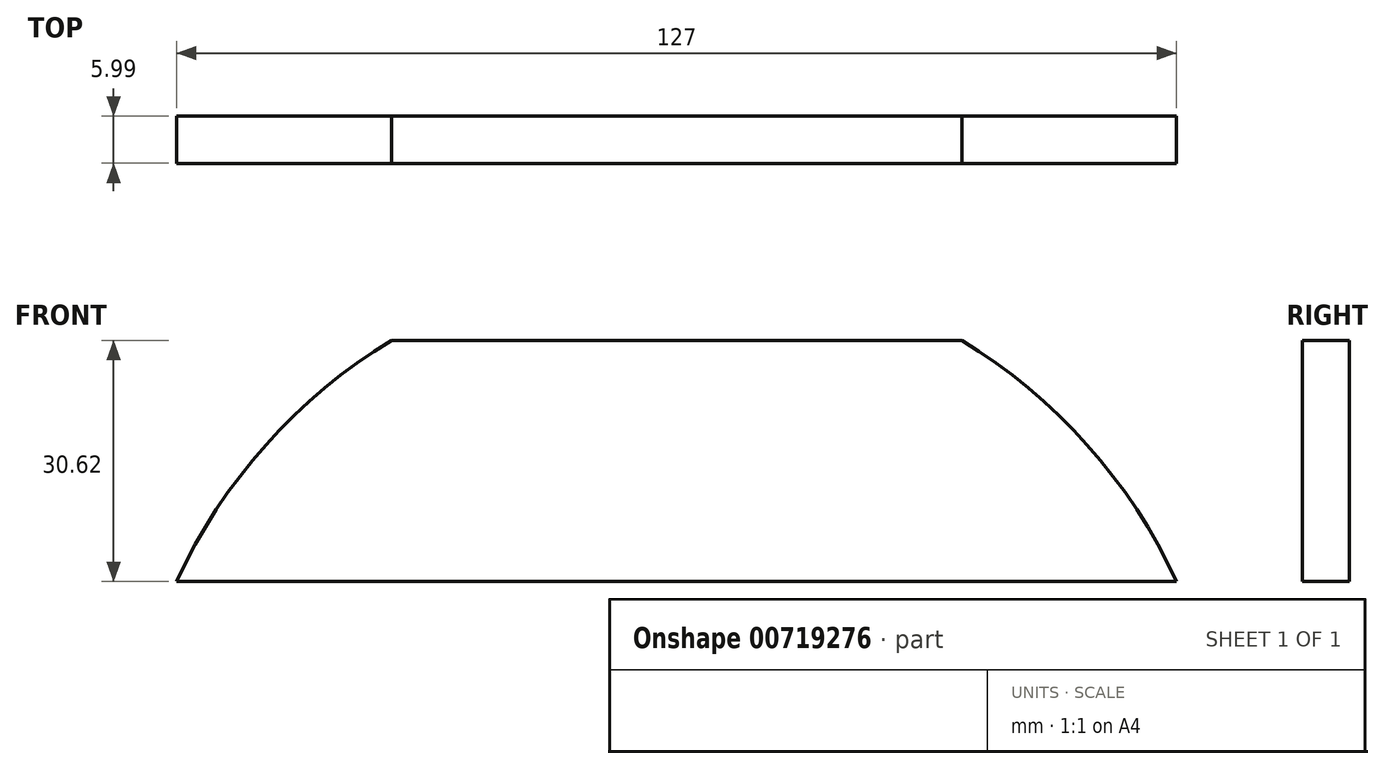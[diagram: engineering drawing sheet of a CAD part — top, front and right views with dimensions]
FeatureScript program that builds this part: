
annotation { "Feature Type Name" : "Feature", "Feature Type Description" : "" }
export const myFeature = defineFeature(function(context is Context, id is Id, definition is map)
    precondition{}
    {
        {
            var Q0;
            Q0=qCreatedBy(makeId("Front.planeOp"),FACE);
            var sketch = newSketch(context, id + "F0", { "sketchPlane" : qUnion([Q0])});
            skLineSegment(sketch, "E0", {"start": v(0, 0) * mm, "end": v(0, 29.1) * mm, "construction": true});
            skLineSegment(sketch, "E1", {"start": v(-63.5, 29.1) * mm, "end": v(-15.24, 29.1) * mm});
            skLineSegment(sketch, "E2", {"start": v(63.5, 29.1) * mm, "end": v(15.24, 29.1) * mm});
            skArc(sketch, "E3", {"start": v(63.5, 29.1) * mm, "mid": v(52.16, 46.46) * mm, "end": v(36.22, 59.72) * mm});
            skLineSegment(sketch, "E4", {"start": v(-36.22, 59.72) * mm, "end": v(36.22, 59.72) * mm});
            skArc(sketch, "E5.trimOffspring", {"start": v(-36.22, 59.72) * mm, "mid": v(-52.16, 46.46) * mm, "end": v(-63.5, 29.1) * mm});
            skLineSegment(sketch, "E6", {"start": v(-15.24, 29.1) * mm, "end": v(15.24, 29.1) * mm});
            skSolve(sketch);
        }
        {
            var Q0;
            Q0=makeQuery(id+"F0.imprint","IMPRINT",FACE,{"disambiguationData":[TD([[makeQuery(id+"F0.imprint","IMPRINT",EDGE,{"derivedFrom":sQuery(id+"F0.wireOp",EDGE,"E1")}),1.0]])]});
            extrude(context, id + "F1", {"entities" : qUnion([Q0]), "depth" : 6 * mm, "offsetDistance" : 25.4 * mm});
        }
    });
